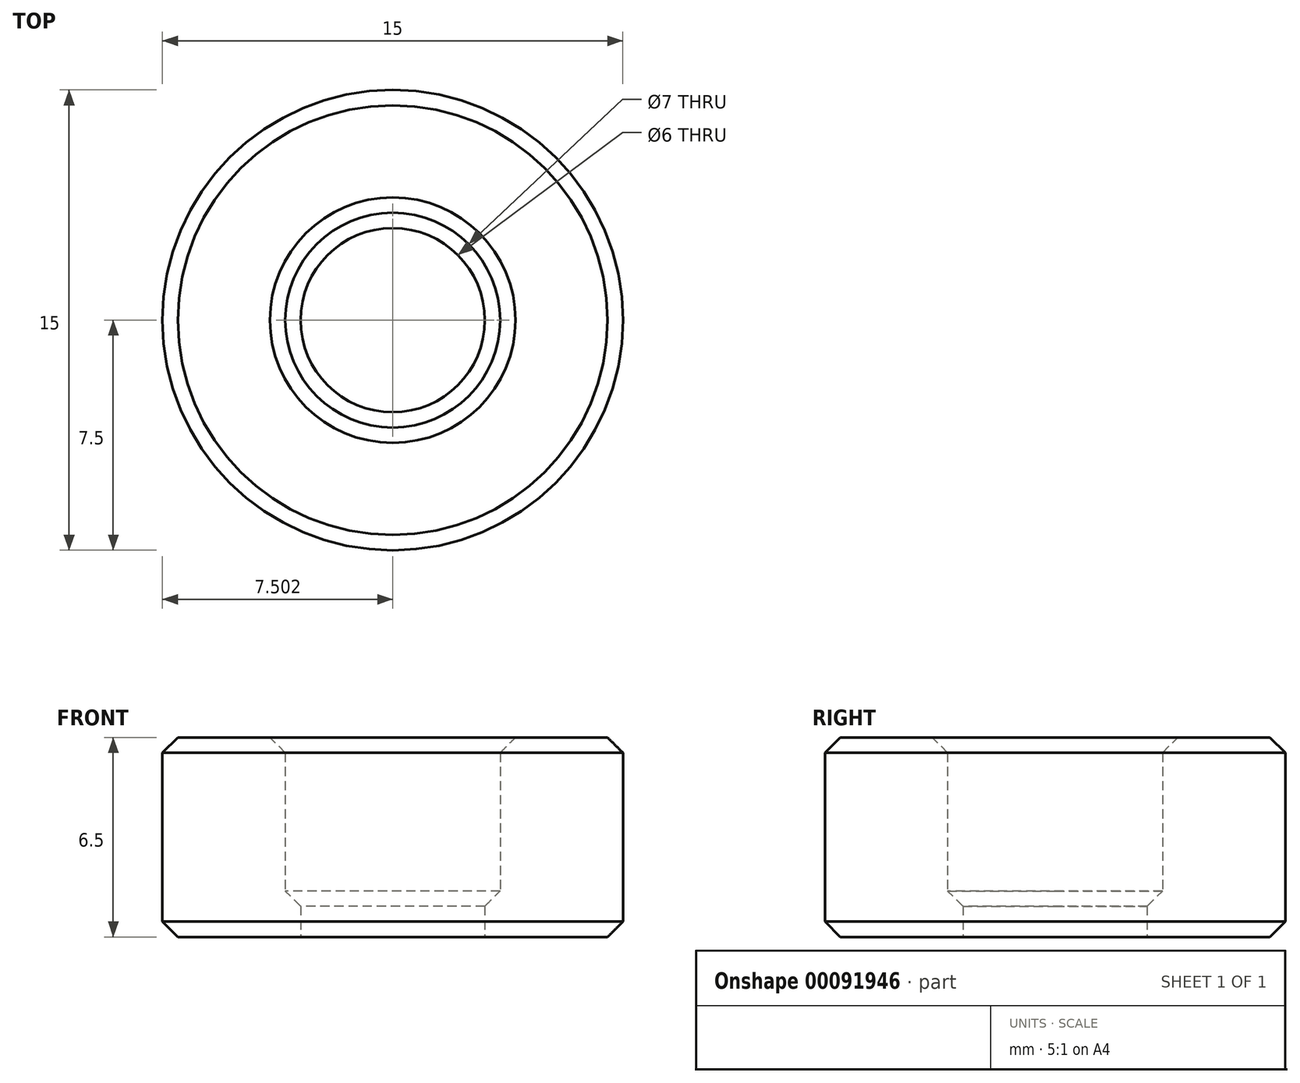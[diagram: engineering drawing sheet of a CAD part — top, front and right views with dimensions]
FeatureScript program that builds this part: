
annotation { "Feature Type Name" : "Feature", "Feature Type Description" : "" }
export const myFeature = defineFeature(function(context is Context, id is Id, definition is map)
    precondition{}
    {
        {
            var Q0;
            Q0=qCreatedBy(makeId("Top.planeOp"),FACE);
            var sketch = newSketch(context, id + "F0", { "sketchPlane" : qUnion([Q0])});
            skCircle(sketch, "E0", {"center": v(-72.28, 42.18) * mm, "radius": 7.5 * mm});
            skCircle(sketch, "E1", {"center": v(-72.28, 42.18) * mm, "radius": 3.5 * mm});
            skCircle(sketch, "E2", {"center": v(-72.28, 42.18) * mm, "radius": 3 * mm});
            skSolve(sketch);
        }
        {
            var Q0;
            Q0=makeQuery(id+"F0.imprint","IMPRINT",FACE,{"disambiguationData":[TD([[makeQuery(id+"F0.imprint","IMPRINT",EDGE,{"derivedFrom":sQuery(id+"F0.wireOp",EDGE,"E0")}),1.0]])]});
            extrude(context, id + "F1", {"entities" : qUnion([Q0]), "depth" : 6.5 * mm});
        }
        {
            var Q0;
            Q0=makeQuery(id+"F0.imprint","IMPRINT",FACE,{"disambiguationData":[TD([[makeQuery(id+"F0.imprint","IMPRINT",EDGE,{"derivedFrom":sQuery(id+"F0.wireOp",EDGE,"E1")}),1.0]])]});
            extrude(context, id + "F2", {"entities" : qUnion([Q0]), "operationType" : NewBodyOperationType.ADD, "depth" : 1.5 * mm});
        }
        {
            var Q0;
            Q0=makeQuery(id+"F1.opExtrude","CAP_EDGE",EDGE,{"disambiguationData":[OSD([sQuery(id+"F0.wireOp",EDGE,"E0")])],"isStart":false});
            var Q1;
            Q1=makeQuery(id+"F1.opExtrude","CAP_EDGE",EDGE,{"disambiguationData":[OSD([sQuery(id+"F0.wireOp",EDGE,"E1")])],"isStart":false});
            var Q2;
            Q2=makeQuery(id+"F2.opExtrude","CAP_EDGE",EDGE,{"disambiguationData":[OSD([sQuery(id+"F0.wireOp",EDGE,"E2")])],"isStart":false});
            var Q3;
            Q3=makeQuery(id+"F1.opExtrude","CAP_EDGE",EDGE,{"disambiguationData":[OSD([sQuery(id+"F0.wireOp",EDGE,"E0")])],"isStart":true});
            chamfer(context, id + "F3", {"entities" : qUnion([Q0, Q1, Q2, Q3]), "width" : .5 * mm, "tangentPropagation" : true});
        }
    });
